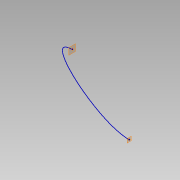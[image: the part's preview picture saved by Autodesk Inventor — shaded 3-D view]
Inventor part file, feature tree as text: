
AUTODESK INVENTOR PART (.ipt)
format: ipt  version: 2019 (Build 230136000, 136)  size: 86,528 bytes
history: native  units: mm
features: other x2, plane x2, sketch x1
ambient origin geometry x8: Origin, YZ Plane, XZ Plane, XY Plane, X Axis, Y Axis, Z Axis, Center Point
feature tree (5):
  other  "Punto de trabajo1"
  other  "Punto de trabajo2"
  plane  "Plano de trabajo1"
  plane  "Plano de trabajo2"
  sketch  "Boceto 3D1"  dims[d0=-10.0mm d1=-0.1mm d2=10.0mm d3=-0.1mm]
